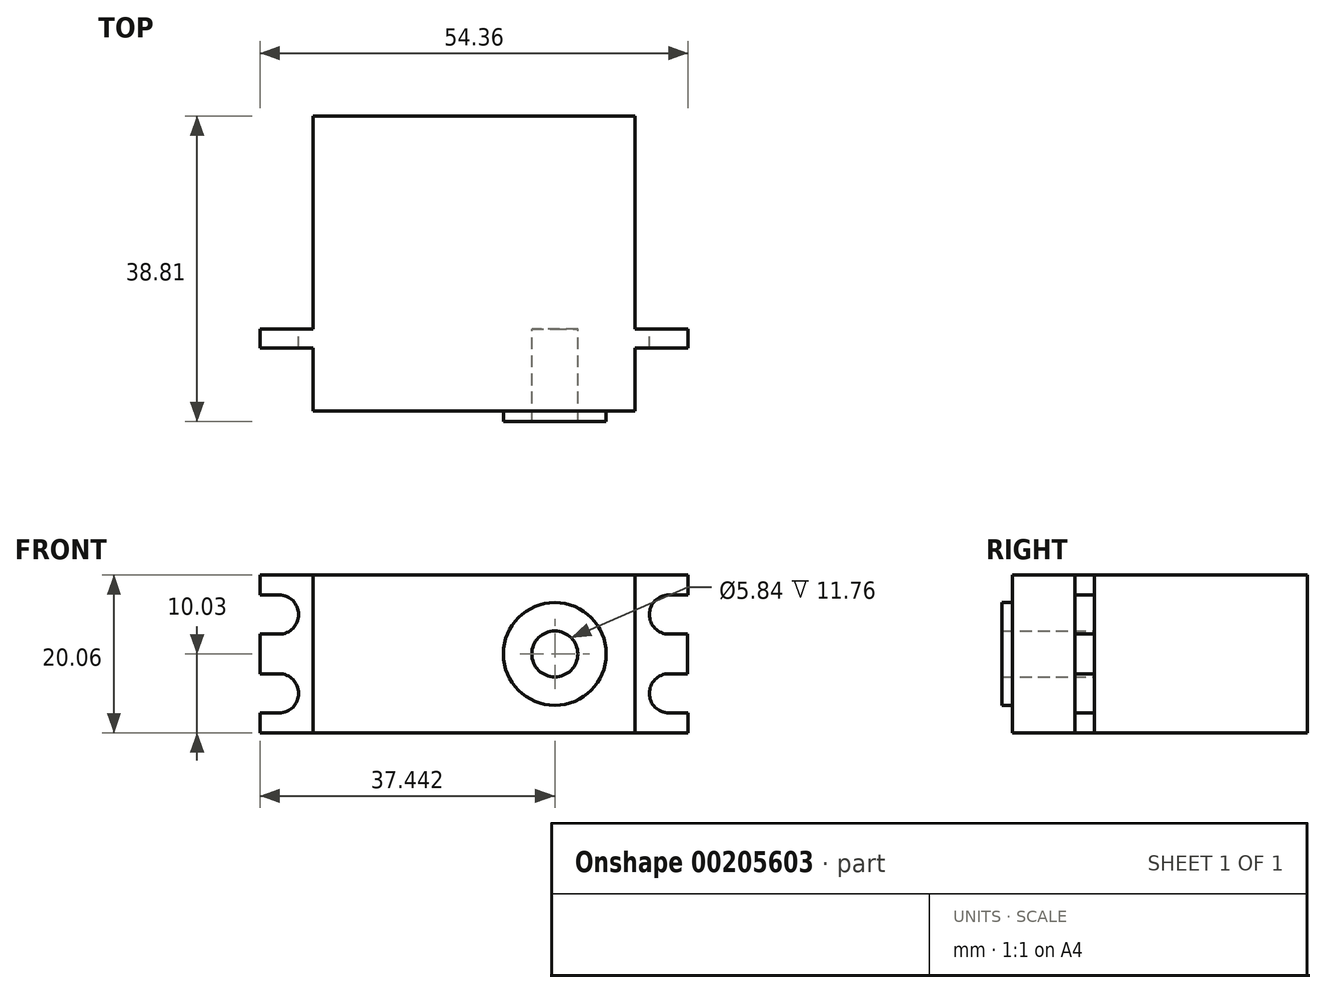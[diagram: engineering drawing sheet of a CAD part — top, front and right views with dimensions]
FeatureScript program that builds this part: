
annotation { "Feature Type Name" : "Feature", "Feature Type Description" : "" }
export const myFeature = defineFeature(function(context is Context, id is Id, definition is map)
    precondition{}
    {
        {
            var Q0;
            Q0=qCreatedBy(makeId("Front.planeOp"),FACE);
            var sketch = newSketch(context, id + "F0", { "sketchPlane" : qUnion([Q0])});
            skLineSegment(sketch, "E0.bottom", {"start": v(20.45, 10.03) * mm, "end": v(-20.45, 10.03) * mm});
            skLineSegment(sketch, "E0.top", {"start": v(20.45, -10.03) * mm, "end": v(-20.45, -10.03) * mm});
            skLineSegment(sketch, "E0.left", {"start": v(20.45, 10.03) * mm, "end": v(20.45, -10.03) * mm});
            skLineSegment(sketch, "E0.right", {"start": v(-20.45, 10.03) * mm, "end": v(-20.45, -10.03) * mm});
            skPoint(sketch, "E0.middle", {"position": v(0, 0) * mm});
            skSolve(sketch);
        }
        {
            var Q0;
            Q0=qSketchRegion(id+"F0",true);
            extrude(context, id + "F1", {"entities" : qUnion([Q0]), "oppositeDirection" : true, "depth" : 27.05 * mm, "hasSecondDirection" : true, "secondDirectionOppositeDirection" : false, "secondDirectionDepth" : 10.4 * mm});
        }
        {
            var Q0;
            Q0=qCreatedBy(makeId("Front.planeOp"),FACE);
            var sketch = newSketch(context, id + "F2", { "sketchPlane" : qUnion([Q0])});
            skLineSegment(sketch, "E1.bottom", {"start": v(27.18, 10.03) * mm, "end": v(-27.18, 10.03) * mm});
            skLineSegment(sketch, "E1.top", {"start": v(27.18, -10.03) * mm, "end": v(-27.18, -10.03) * mm});
            skLineSegment(sketch, "E1.left", {"start": v(27.18, 10.03) * mm, "end": v(27.18, 7.5) * mm});
            skLineSegment(sketch, "E1.right", {"start": v(-27.18, 10.03) * mm, "end": v(-27.18, 7.5) * mm});
            skPoint(sketch, "E1.middle", {"position": v(0, 0) * mm});
            skArc(sketch, "E2", {"start": v(-24.77, -7.5) * mm, "mid": v(-22.28, -5) * mm, "end": v(-24.77, -2.51) * mm});
            skPoint(sketch, "E3.MirrorP", {"position": v(0, 13.61) * mm});
            skLineSegment(sketch, "E4.MirrorCS", {"start": v(24.77, 2.51) * mm, "end": v(27.09, 2.51) * mm});
            skLineSegment(sketch, "E5.MirrorCS", {"start": v(24.77, -2.51) * mm, "end": v(27.09, -2.51) * mm});
            skLineSegment(sketch, "E6.MirrorCS", {"start": v(24.77, -7.5) * mm, "end": v(27.18, -7.5) * mm});
            skLineSegment(sketch, "E7.MirrorCS", {"start": v(24.77, 7.5) * mm, "end": v(27.18, 7.5) * mm});
            skArc(sketch, "E8", {"start": v(24.77, 7.5) * mm, "mid": v(22.28, 5) * mm, "end": v(24.77, 2.51) * mm});
            skArc(sketch, "E9", {"start": v(24.77, -2.51) * mm, "mid": v(22.28, -5) * mm, "end": v(24.77, -7.5) * mm});
            skLineSegment(sketch, "E10", {"start": v(27.18, -7.5) * mm, "end": v(27.18, -10.03) * mm});
            skLineSegment(sketch, "E11", {"start": v(27.09, 2.51) * mm, "end": v(27.09, -2.51) * mm});
            skLineSegment(sketch, "E12.trimOffspring", {"start": v(-27.18, 2.52) * mm, "end": v(-27.18, -2.51) * mm});
            skLineSegment(sketch, "E13.trimOffspring", {"start": v(-27.18, -7.5) * mm, "end": v(-27.18, -10.03) * mm});
            skLineSegment(sketch, "E14", {"start": v(-24.77, 7.5) * mm, "end": v(-27.18, 7.5) * mm});
            skLineSegment(sketch, "E15", {"start": v(-24.77, -2.51) * mm, "end": v(-27.18, -2.51) * mm});
            skLineSegment(sketch, "E16", {"start": v(-24.77, -7.5) * mm, "end": v(-27.18, -7.5) * mm});
            skArc(sketch, "E17.trimOffspring", {"start": v(-24.77, 2.52) * mm, "mid": v(-22.28, 5) * mm, "end": v(-24.77, 7.5) * mm});
            skLineSegment(sketch, "E18", {"start": v(-27.18, 2.52) * mm, "end": v(-24.77, 2.52) * mm});
            skSolve(sketch);
        }
        {
            var Q0;
            Q0=qSketchRegion(id+"F2",true);
            extrude(context, id + "F3", {"entities" : qUnion([Q0]), "operationType" : NewBodyOperationType.ADD, "depth" : 2.44 * mm});
        }
        {
            var Q0;
            Q0=qCreatedBy(makeId("Front.planeOp"),FACE);
            var sketch = newSketch(context, id + "F4", { "sketchPlane" : qUnion([Q0])});
            skCircle(sketch, "E19", {"center": v(10.26, 0) * mm, "radius": 6.53 * mm});
            skSolve(sketch);
        }
        {
            var Q0;
            Q0=qSketchRegion(id+"F4",true);
            extrude(context, id + "F5", {"entities" : qUnion([Q0]), "operationType" : NewBodyOperationType.ADD, "depth" : 11.76 * mm});
        }
        {
            var Q0;
            Q0=qCreatedBy(makeId("Front.planeOp"),FACE);
            var sketch = newSketch(context, id + "F6", { "sketchPlane" : qUnion([Q0])});
            skCircle(sketch, "E20", {"center": v(10.26, 0) * mm, "radius": 2.92 * mm});
            skSolve(sketch);
        }
        {
            var Q0;
            Q0=qSketchRegion(id+"F6",true);
            extrude(context, id + "F7", {"entities" : qUnion([Q0]), "operationType" : NewBodyOperationType.REMOVE, "depth" : 14.2 * mm});
        }
    });
